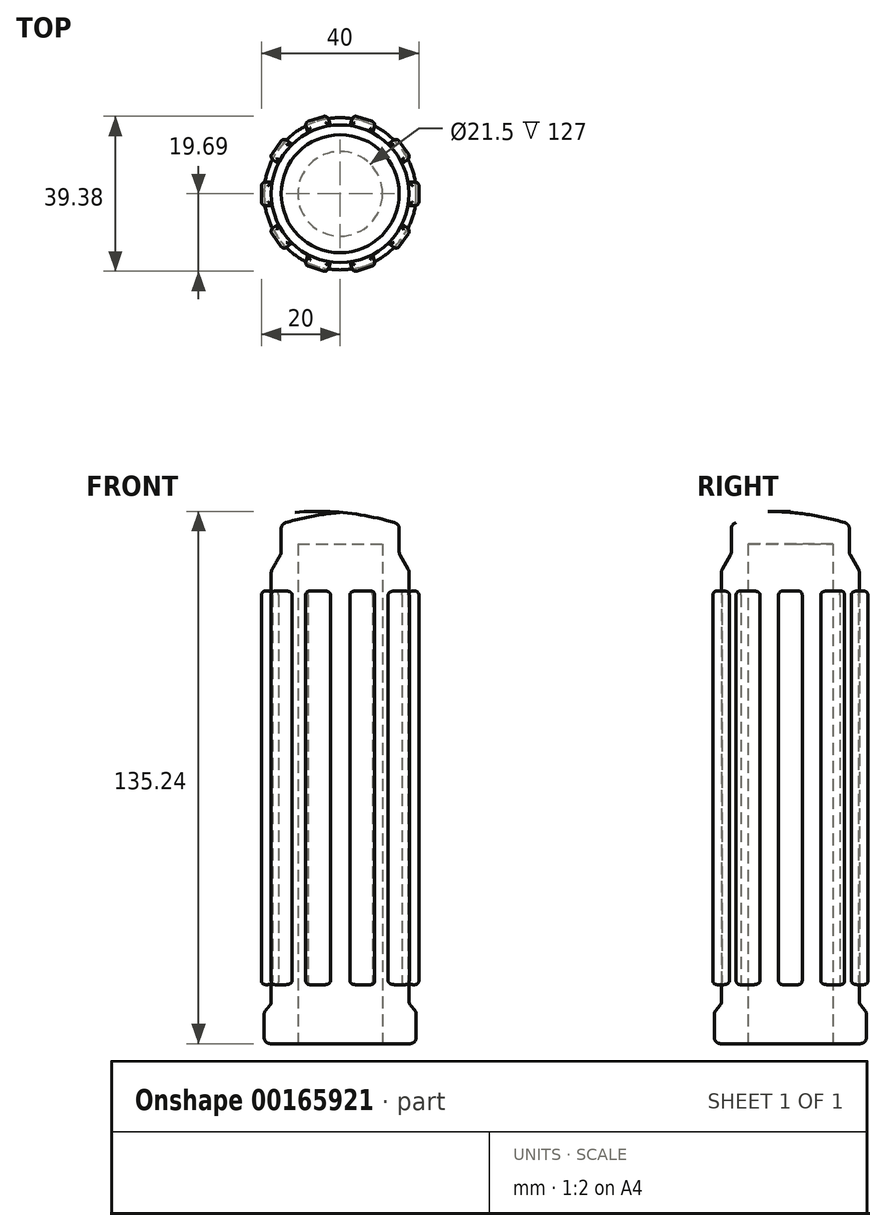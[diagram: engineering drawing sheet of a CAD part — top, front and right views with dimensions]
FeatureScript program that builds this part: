
annotation { "Feature Type Name" : "Feature", "Feature Type Description" : "" }
export const myFeature = defineFeature(function(context is Context, id is Id, definition is map)
    precondition{}
    {
        {
            var Q0;
            Q0=qCreatedBy(makeId("Front.planeOp"),FACE);
            var sketch = newSketch(context, id + "F0", { "sketchPlane" : qUnion([Q0])});
            skLineSegment(sketch, "E0", {"start": v(0, 0) * mm, "end": v(0, 155.81) * mm, "construction": true});
            skLineSegment(sketch, "E1", {"start": v(10.75, 0) * mm, "end": v(10.75, 127) * mm});
            skLineSegment(sketch, "E2", {"start": v(10.75, 127) * mm, "end": v(0, 127) * mm});
            skLineSegment(sketch, "E3", {"start": v(0, 127) * mm, "end": v(0, 135) * mm});
            skArc(sketch, "E4", {"start": v(15, 132) * mm, "mid": v(7.58, 133.93) * mm, "end": v(0, 135) * mm});
            skLineSegment(sketch, "E5", {"start": v(17.5, 10.17) * mm, "end": v(19.33, 8) * mm});
            skLineSegment(sketch, "E6", {"start": v(19.33, 8) * mm, "end": v(19.33, 0) * mm});
            skLineSegment(sketch, "E7", {"start": v(19.33, 0) * mm, "end": v(10.75, 0) * mm});
            skLineSegment(sketch, "E8", {"start": v(15, 132) * mm, "end": v(15, 124.5) * mm});
            skLineSegment(sketch, "E9", {"start": v(15, 124.5) * mm, "end": v(17.5, 120.17) * mm});
            skLineSegment(sketch, "E10", {"start": v(17.5, 120.17) * mm, "end": v(17.5, 10.17) * mm});
            skSolve(sketch);
        }
        {
            var Q0;
            Q0=qSketchRegion(id+"F0",true);
            var Q1;
            Q1=sQuery(id+"F0.wireOp",EDGE,"E0");
            revolve(context, id + "F1", {"entities" : qUnion([Q0]), "axis" : qUnion([Q1]), "revolveType" : RevolveType.FULL});
        }
        {
            var Q0;
            Q0=makeQuery(id+"F1.opRevolve","SWEPT_EDGE",EDGE,{"disambiguationData":[OSD([sQuery(id+"F0.wireOp",EDGE,"E4"),sQuery(id+"F0.wireOp",EDGE,"E8")])]});
            var Q1;
            Q1=makeQuery(id+"F1.opRevolve","SWEPT_EDGE",EDGE,{"disambiguationData":[OSD([sQuery(id+"F0.wireOp",EDGE,"E9"),sQuery(id+"F0.wireOp",EDGE,"E10")])]});
            var Q2;
            Q2=makeQuery(id+"F1.opRevolve","SWEPT_EDGE",EDGE,{"disambiguationData":[OSD([sQuery(id+"F0.wireOp",EDGE,"E8"),sQuery(id+"F0.wireOp",EDGE,"E9")])]});
            var Q3;
            Q3=makeQuery(id+"F1.opRevolve","SWEPT_EDGE",EDGE,{"disambiguationData":[OSD([sQuery(id+"F0.wireOp",EDGE,"E5"),sQuery(id+"F0.wireOp",EDGE,"E10")])]});
            var Q4;
            Q4=makeQuery(id+"F1.opRevolve","SWEPT_EDGE",EDGE,{"disambiguationData":[OSD([sQuery(id+"F0.wireOp",EDGE,"E5"),sQuery(id+"F0.wireOp",EDGE,"E6")])]});
            var Q5;
            Q5=makeQuery(id+"F1.opRevolve","SWEPT_EDGE",EDGE,{"disambiguationData":[OSD([sQuery(id+"F0.wireOp",EDGE,"E6"),sQuery(id+"F0.wireOp",EDGE,"E7")])]});
            fillet(context, id + "F2", {"entities" : qUnion([Q0, Q1, Q2, Q3, Q4, Q5]), "radius" : 1.6 * mm, "tangentPropagation" : true, "allowEdgeOverflow" : false});
        }
        {
            var Q0;
            Q0=qCreatedBy(makeId("Right.planeOp"),FACE);
            cPlane(context, id + "F3", {"entities" : qUnion([Q0]), "cplaneType" : CPlaneType.OFFSET, "offset" : 20 * mm, "width" : 150 * mm, "height" : 150 * mm});
        }
        {
            var Q0;
            Q0=qCreatedBy(id+"F3.planeOp",FACE);
            var sketch = newSketch(context, id + "F4", { "sketchPlane" : qUnion([Q0])});
            skLineSegment(sketch, "E11.bottom", {"start": v(-3, 115) * mm, "end": v(3, 115) * mm});
            skLineSegment(sketch, "E11.top", {"start": v(-3, 15) * mm, "end": v(3, 15) * mm});
            skLineSegment(sketch, "E11.left", {"start": v(-3, 115) * mm, "end": v(-3, 15) * mm});
            skLineSegment(sketch, "E11.right", {"start": v(3, 115) * mm, "end": v(3, 15) * mm});
            skSolve(sketch);
        }
        {
            var Q0;
            Q0=qSketchRegion(id+"F4",true);
            var Q1;
            Q1=makeQuery(id+"F1.opRevolve","SWEPT_FACE",FACE,{"disambiguationData":[OSD([sQuery(id+"F0.wireOp",EDGE,"E10")])]});
            extrude(context, id + "F5", {"entities" : qUnion([Q0]), "endBound" : BoundingType.UP_TO_SURFACE, "oppositeDirection" : true, "endBoundEntityFace" : qUnion([Q1]), "depth" : 25 * mm});
        }
        {
            var Q0;
            Q0=makeQuery(id+"F5.opExtrude","CAP_FACE",FACE,{"disambiguationData":[OSD([sQuery(id+"F4.wireOp",EDGE,"E11.bottom"),sQuery(id+"F4.wireOp",EDGE,"E11.top"),sQuery(id+"F4.wireOp",EDGE,"E11.left"),sQuery(id+"F4.wireOp",EDGE,"E11.right")])],"isStart":true});
            var Q1;
            Q1=makeQuery(id+"F5.opExtrude","TWEAK_EDGE",EDGE,{"derivedFrom":[makeQuery(id+"F1.opRevolve","SWEPT_FACE",FACE,{"disambiguationData":[OSD([sQuery(id+"F0.wireOp",EDGE,"E10")])]}),makeQuery(id+"F4.imprint","IMPRINT",EDGE,{"derivedFrom":sQuery(id+"F4.wireOp",EDGE,"E11.right")})]});
            var Q2;
            Q2=makeQuery(id+"F5.opExtrude","SWEPT_FACE",FACE,{"disambiguationData":[OSD([sQuery(id+"F4.wireOp",EDGE,"E11.bottom")])]});
            var Q3;
            Q3=makeQuery(id+"F5.opExtrude","SWEPT_FACE",FACE,{"disambiguationData":[OSD([sQuery(id+"F4.wireOp",EDGE,"E11.top")])]});
            fillet(context, id + "F6", {"entities" : qUnion([Q0, Q1, Q2, Q3]), "radius" : 1 * mm, "tangentPropagation" : true, "allowEdgeOverflow" : false});
        }
        {
            var Q0;
            Q0=makeQuery(id+"F5.opExtrude","SWEPT_BODY",BODY,{"disambiguationData":[OSD([sQuery(id+"F4.wireOp",EDGE,"E11.bottom"),sQuery(id+"F4.wireOp",EDGE,"E11.top"),sQuery(id+"F4.wireOp",EDGE,"E11.left"),sQuery(id+"F4.wireOp",EDGE,"E11.right")])]});
            var Q1;
            {var subQ0=sQuery(id+"F0.wireOp",EDGE,"E7");Q1=makeQuery(id+"F2.opFillet","BLEND_EDGE",EDGE,{"blendedFrom":[makeQuery(id+"F1.opRevolve","SWEPT_EDGE",EDGE,{"disambiguationData":[OSD([sQuery(id+"F0.wireOp",EDGE,"E6"),subQ0])]}),makeQuery(id+"F1.opRevolve","SWEPT_FACE",FACE,{"disambiguationData":[OSD([subQ0])]})],"blendedInto":[makeQuery(id+"F1.opRevolve","SWEPT_FACE",FACE,{"disambiguationData":[OSD([subQ0])]})]});}
            circularPattern(context, id + "F7", {"entities" : qUnion([Q0]), "axis" : qUnion([Q1]), "angle" : 360 * degree, "instanceCount" : 10, "equalSpace" : true});
        }
    });
